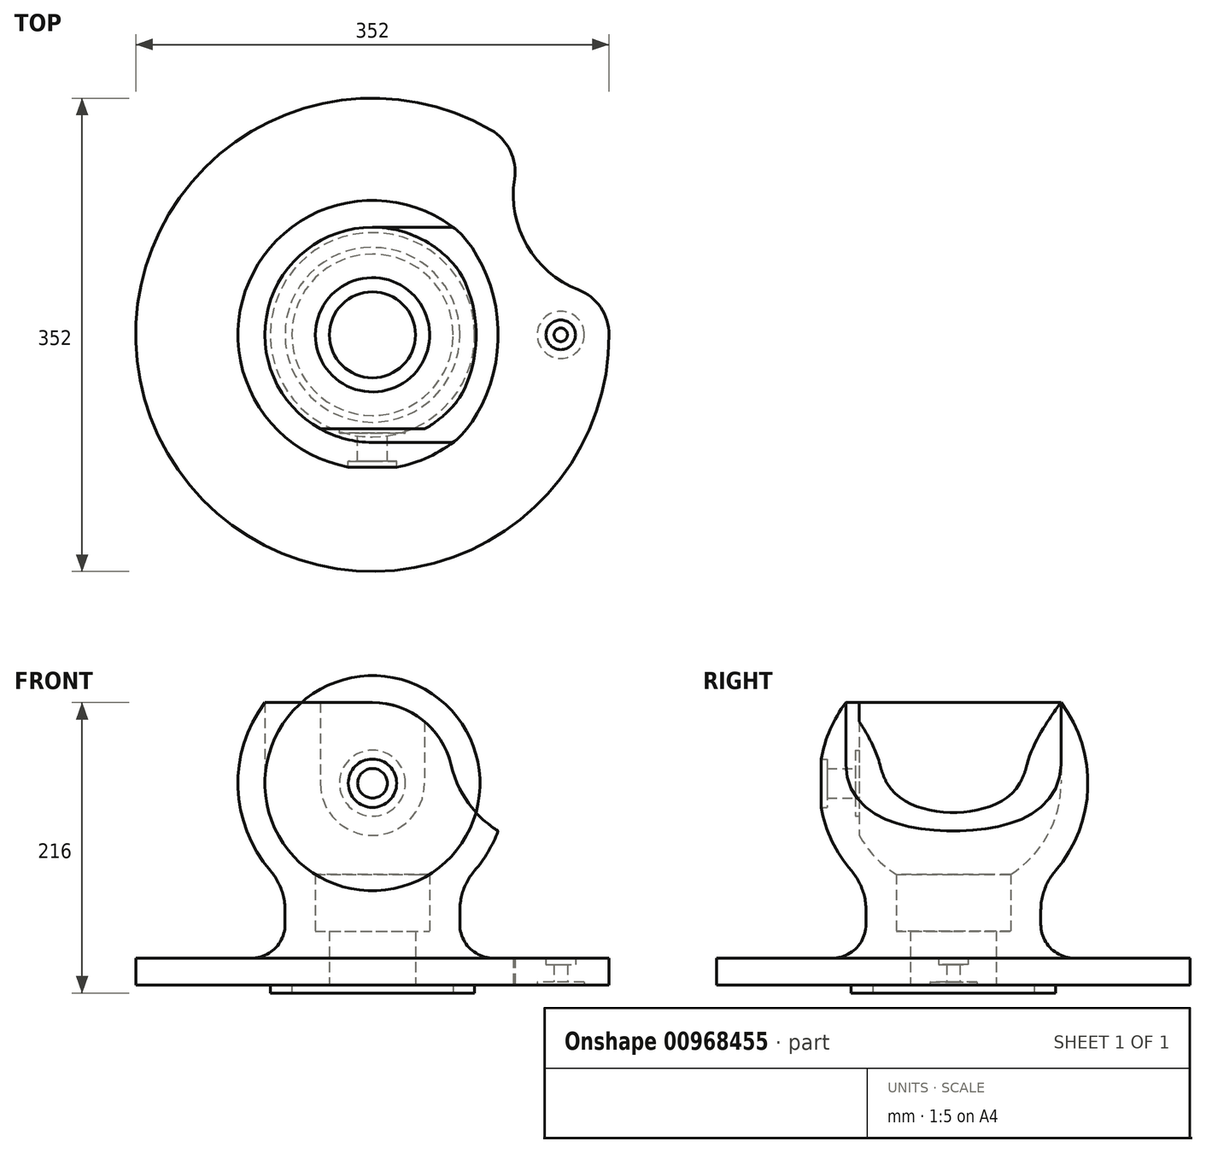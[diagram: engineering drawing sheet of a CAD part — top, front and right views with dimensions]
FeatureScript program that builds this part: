
annotation { "Feature Type Name" : "Feature", "Feature Type Description" : "" }
export const myFeature = defineFeature(function(context is Context, id is Id, definition is map)
    precondition{}
    {
        {
            var Q0;
            Q0=qCreatedBy(makeId("Front.planeOp"),FACE);
            cPlane(context, id + "F0", {"entities" : qUnion([Q0]), "cplaneType" : CPlaneType.OFFSET, "offset" : 100 * mm, "width" : 150 * mm, "height" : 150 * mm});
        }
        {
            var Q0;
            Q0=qCreatedBy(makeId("Front.planeOp"),FACE);
            var sketch = newSketch(context, id + "F1", { "sketchPlane" : qUnion([Q0])});
            skLineSegment(sketch, "E0", {"start": v(32, 0) * mm, "end": v(60, 0) * mm});
            skLineSegment(sketch, "E1", {"start": v(60, 0) * mm, "end": v(60, -6) * mm});
            skLineSegment(sketch, "E2", {"start": v(60, -6) * mm, "end": v(76, -6) * mm});
            skLineSegment(sketch, "E3", {"start": v(76, -6) * mm, "end": v(76, 0) * mm});
            skLineSegment(sketch, "E4", {"start": v(76, 0) * mm, "end": v(176, 0) * mm});
            skLineSegment(sketch, "E5", {"start": v(176, 0) * mm, "end": v(176, 20) * mm});
            skLineSegment(sketch, "E6", {"start": v(176, 20) * mm, "end": v(90, 20) * mm});
            skLineSegment(sketch, "E7", {"start": v(65, 45) * mm, "end": v(65, 55.53) * mm});
            skArc(sketch, "E8", {"start": v(75.86, 84.85) * mm, "mid": v(99.95, 146.7) * mm, "end": v(80, 210) * mm});
            skLineSegment(sketch, "E9", {"start": v(32, 0) * mm, "end": v(32, 40) * mm});
            skLineSegment(sketch, "E10", {"start": v(32, 40) * mm, "end": v(42.5, 40) * mm});
            skLineSegment(sketch, "E11", {"start": v(42.5, 40) * mm, "end": v(42.5, 82.22) * mm});
            skLineSegment(sketch, "E12", {"start": v(80, 210) * mm, "end": v(80, 210) * mm});
            skPoint(sketch, "E13.visualSharp", {"position": v(65, 20) * mm});
            skArc(sketch, "E13.filletArc", {"start": v(65, 45) * mm, "mid": v(72.32, 27.32) * mm, "end": v(90, 20) * mm});
            skPoint(sketch, "E14.visualSharp", {"position": v(65, 74) * mm});
            skArc(sketch, "E14.filletArc", {"start": v(75.86, 84.85) * mm, "mid": v(67.8, 71.16) * mm, "end": v(65, 55.53) * mm});
            skLineSegment(sketch, "E15", {"start": v(0, 0) * mm, "end": v(0, 210) * mm, "construction": true});
            skLineSegment(sketch, "E16", {"start": v(80, 210) * mm, "end": v(80, 150) * mm});
            skArc(sketch, "E17", {"start": v(42.5, 82.22) * mm, "mid": v(70, 111.27) * mm, "end": v(80, 150) * mm});
            skPoint(sketch, "E18.orphan", {"position": v(42.5, 210) * mm});
            skSolve(sketch);
        }
        {
            var Q0;
            Q0=qCreatedBy(makeId("Front.planeOp"),FACE);
            var sketch = newSketch(context, id + "F2", { "sketchPlane" : qUnion([Q0])});
            skArc(sketch, "E19", {"start": v(-40, 150) * mm, "mid": v(0, 110) * mm, "end": v(40, 150) * mm});
            skLineSegment(sketch, "E20", {"start": v(-40, 150) * mm, "end": v(-40, 210) * mm});
            skLineSegment(sketch, "E21", {"start": v(-40, 210) * mm, "end": v(40, 210) * mm});
            skLineSegment(sketch, "E22", {"start": v(40, 210) * mm, "end": v(40, 150) * mm});
            skLineSegment(sketch, "E23.0", {"start": v(80, 210) * mm, "end": v(80, 150) * mm, "construction": true});
            skSolve(sketch);
        }
        {
            var Q0;
            Q0=makeQuery(id+"F1.imprint","IMPRINT",FACE,{"disambiguationData":[TD([[makeQuery(id+"F1.imprint","IMPRINT",EDGE,{"derivedFrom":sQuery(id+"F1.wireOp",EDGE,"E0")}),1.0]])]});
            var Q1;
            Q1=sQuery(id+"F1.wireOp",EDGE,"E15");
            revolve(context, id + "F3", {"surfaceOperationType" : NewSurfaceOperationType.NEW, "entities" : qUnion([Q0]), "axis" : qUnion([Q1]), "revolveType" : RevolveType.FULL});
        }
        {
            var Q0;
            Q0=makeQuery(id+"F2.imprint","IMPRINT",FACE,{"disambiguationData":[TD([[makeQuery(id+"F2.imprint","IMPRINT",EDGE,{"derivedFrom":sQuery(id+"F2.wireOp",EDGE,"E19")}),1.0]])]});
            var Q1;
            Q1=makeQuery(id+"F3.opRevolve","SWEPT_FACE",FACE,{"disambiguationData":[OSD([sQuery(id+"F1.wireOp",EDGE,"E16")])]});
            extrude(context, id + "F4", {"entities" : qUnion([Q0]), "operationType" : NewBodyOperationType.ADD, "endBound" : BoundingType.UP_TO_SURFACE, "depth" : 25 * mm, "endBoundEntityFace" : qUnion([Q1]), "offsetDistance" : 25 * mm, "hasSecondDirection" : true, "secondDirectionOppositeDirection" : false, "secondDirectionDepth" : 70 * mm});
        }
        {
            var Q0;
            Q0=makeQuery(id+"F4.opExtrude","CAP_FACE",FACE,{"disambiguationData":[OSD([sQuery(id+"F2.wireOp",EDGE,"E19"),sQuery(id+"F2.wireOp",EDGE,"E20"),sQuery(id+"F2.wireOp",EDGE,"E21"),sQuery(id+"F2.wireOp",EDGE,"E22")])],"isStart":true});
            var sketch = newSketch(context, id + "F5", { "sketchPlane" : qUnion([Q0])});
            skPoint(sketch, "E24.0", {"position": v(0, 150) * mm});
            skCircle(sketch, "E25", {"center": v(0, 150) * mm, "radius": 24.5 * mm});
            skSolve(sketch);
        }
        {
            var Q0;
            Q0=qCreatedBy(id+"F0.planeOp",FACE);
            var sketch = newSketch(context, id + "F6", { "sketchPlane" : qUnion([Q0])});
            skPoint(sketch, "E26.0", {"position": v(0, 150) * mm});
            skSolve(sketch);
        }
        {
            var Q0;
            Q0=makeQuery(id+"F5.imprint","IMPRINT",FACE,{"disambiguationData":[TD([[makeQuery(id+"F5.imprint","IMPRINT",EDGE,{"derivedFrom":sQuery(id+"F5.wireOp",EDGE,"E25")}),1.0]])]});
            extrude(context, id + "F7", {"entities" : qUnion([Q0]), "operationType" : NewBodyOperationType.REMOVE, "oppositeDirection" : true, "depth" : 3 * mm, "offsetDistance" : 25 * mm});
        }
        {
            var Q0;
            Q0=sQuery(id+"F6.wireOp",VERTEX,"E26.0");
            var Q1;
            Q1=makeQuery(id+"F3.opRevolve","SWEPT_BODY",BODY,{"disambiguationData":[OSD([sQuery(id+"F1.wireOp",EDGE,"E0"),sQuery(id+"F1.wireOp",EDGE,"E1"),sQuery(id+"F1.wireOp",EDGE,"E2"),sQuery(id+"F1.wireOp",EDGE,"E3"),sQuery(id+"F1.wireOp",EDGE,"E4"),sQuery(id+"F1.wireOp",EDGE,"E5"),sQuery(id+"F1.wireOp",EDGE,"E6"),sQuery(id+"F1.wireOp",EDGE,"E7"),sQuery(id+"F1.wireOp",EDGE,"E8"),sQuery(id+"F1.wireOp",EDGE,"E9"),sQuery(id+"F1.wireOp",EDGE,"E10"),sQuery(id+"F1.wireOp",EDGE,"E11"),sQuery(id+"F1.wireOp",EDGE,"E12"),sQuery(id+"F1.wireOp",EDGE,"E13.filletArc"),sQuery(id+"F1.wireOp",EDGE,"E14.filletArc"),sQuery(id+"F1.wireOp",EDGE,"E16"),sQuery(id+"F1.wireOp",EDGE,"E17")])]});
            hole(context, id + "F8", {"style" : HoleStyle.C_BORE, "endStyle" : HoleEndStyle.BLIND, "holeDiameter" : 22 * mm, "cBoreDiameter" : 36 * mm, "cBoreDepth" : 6 * mm, "majorDiameter" : 5 * mm, "holeDepth" : 50 * mm, "isTappedThrough" : true, "tappedDepth" : 29.75 * mm, "tapClearance" : 3, "startFromSketch" : true, "locations" : qUnion([Q0]), "scope" : qUnion([Q1])});
        }
        {
            var Q0;
            Q0=qCreatedBy(makeId("Front.planeOp"),FACE);
            var sketch = newSketch(context, id + "F9", { "sketchPlane" : qUnion([Q0])});
            skArc(sketch, "E27", {"start": v(58.41, 163.71) * mm, "mid": v(0, 210) * mm, "end": v(-58.41, 163.71) * mm});
            skArc(sketch, "E28", {"start": v(58.41, 163.71) * mm, "mid": v(84.18, 121.3) * mm, "end": v(130, 102.25) * mm});
            skArc(sketch, "E29.MirrorCS", {"start": v(-58.41, 163.71) * mm, "mid": v(-84.18, 121.3) * mm, "end": v(-130, 102.25) * mm});
            skLineSegment(sketch, "E30", {"start": v(130, 102.25) * mm, "end": v(130, 210) * mm});
            skLineSegment(sketch, "E31", {"start": v(130, 210) * mm, "end": v(-130, 210) * mm});
            skLineSegment(sketch, "E32", {"start": v(-130, 210) * mm, "end": v(-130, 102.25) * mm});
            skSolve(sketch);
        }
        {
            var Q0;
            {var subQ0=sQuery(id+"F9.wireOp",EDGE,"E28");Q0=makeQuery(id+"F9.imprint","IMPRINT",FACE,{"disambiguationData":[TD([[makeQuery(id+"F9.imprint","IMPRINT",EDGE,{"derivedFrom":subQ0}),1.0]])]});}
            var Q1;
            {var subQ0=sQuery(id+"F9.wireOp",EDGE,"E29.MirrorCS");Q1=makeQuery(id+"F9.imprint","IMPRINT",FACE,{"disambiguationData":[TD([[makeQuery(id+"F9.imprint","IMPRINT",EDGE,{"derivedFrom":subQ0}),-1.0]])]});}
            extrude(context, id + "F10", {"entities" : qUnion([Q0, Q1]), "operationType" : NewBodyOperationType.REMOVE, "oppositeDirection" : true, "depth" : 200 * mm, "offsetDistance" : 25 * mm, "symmetric" : true});
        }
        {
            var Q0;
            Q0=qCreatedBy(makeId("Top.planeOp"),FACE);
            var sketch = newSketch(context, id + "F11", { "sketchPlane" : qUnion([Q0])});
            skArc(sketch, "E33", {"start": v(176, 0) * mm, "mid": v(169.72, 20.3) * mm, "end": v(153.09, 33.54) * mm});
            skArc(sketch, "E34", {"start": v(105.59, 115.8) * mm, "mid": v(102.45, 136.83) * mm, "end": v(88, 152.42) * mm});
            skLineSegment(sketch, "E35", {"start": v(70, 121.24) * mm, "end": v(0, 0) * mm, "construction": true});
            skArc(sketch, "E36", {"start": v(105.59, 115.8) * mm, "mid": v(114.9, 66.34) * mm, "end": v(153.09, 33.54) * mm});
            skArc(sketch, "E37.0", {"start": v(176, 0) * mm, "mid": v(152.42, 88) * mm, "end": v(88, 152.42) * mm});
            skCircle(sketch, "E38", {"center": v(140, 0) * mm, "radius": 17.5 * mm});
            skSolve(sketch);
        }
        {
            var Q0;
            Q0=makeQuery(id+"F11.imprint","IMPRINT",FACE,{"disambiguationData":[TD([[makeQuery(id+"F11.imprint","IMPRINT",EDGE,{"derivedFrom":sQuery(id+"F11.wireOp",EDGE,"E33")}),-1.0]])]});
            extrude(context, id + "F12", {"entities" : qUnion([Q0]), "operationType" : NewBodyOperationType.REMOVE, "endBound" : BoundingType.THROUGH_ALL, "depth" : 25 * mm, "offsetDistance" : 25 * mm});
        }
        {
            var Q0;
            Q0=makeQuery(id+"F11.imprint","IMPRINT",FACE,{"disambiguationData":[TD([[makeQuery(id+"F11.imprint","IMPRINT",EDGE,{"derivedFrom":sQuery(id+"F11.wireOp",EDGE,"E38")}),1.0]])]});
            extrude(context, id + "F13", {"entities" : qUnion([Q0]), "operationType" : NewBodyOperationType.REMOVE, "depth" : 2 * mm, "offsetDistance" : 25 * mm});
        }
        {
            var Q0;
            Q0=makeQuery(id+"F3.opRevolve","SWEPT_FACE",FACE,{"disambiguationData":[OSD([sQuery(id+"F1.wireOp",EDGE,"E6")])]});
            var sketch = newSketch(context, id + "F14", { "sketchPlane" : qUnion([Q0])});
            skPoint(sketch, "E39.0", {"position": v(140, 0) * mm});
            skSolve(sketch);
        }
        {
            var Q0;
            Q0=sQuery(id+"F14.wireOp",VERTEX,"E39.0");
            var Q1;
            Q1=makeQuery(id+"F3.opRevolve","SWEPT_BODY",BODY,{"disambiguationData":[OSD([sQuery(id+"F1.wireOp",EDGE,"E0"),sQuery(id+"F1.wireOp",EDGE,"E1"),sQuery(id+"F1.wireOp",EDGE,"E2"),sQuery(id+"F1.wireOp",EDGE,"E3"),sQuery(id+"F1.wireOp",EDGE,"E4"),sQuery(id+"F1.wireOp",EDGE,"E5"),sQuery(id+"F1.wireOp",EDGE,"E6"),sQuery(id+"F1.wireOp",EDGE,"E7"),sQuery(id+"F1.wireOp",EDGE,"E8"),sQuery(id+"F1.wireOp",EDGE,"E9"),sQuery(id+"F1.wireOp",EDGE,"E10"),sQuery(id+"F1.wireOp",EDGE,"E11"),sQuery(id+"F1.wireOp",EDGE,"E13.filletArc"),sQuery(id+"F1.wireOp",EDGE,"E14.filletArc"),sQuery(id+"F1.wireOp",EDGE,"E16"),sQuery(id+"F1.wireOp",EDGE,"E17")])]});
            hole(context, id + "F15", {"style" : HoleStyle.C_BORE, "endStyle" : HoleEndStyle.THROUGH, "holeDiameter" : 10 * mm, "cBoreDiameter" : 22 * mm, "cBoreDepth" : 5 * mm, "majorDiameter" : 5 * mm, "isTappedThrough" : true, "tappedDepth" : 29.75 * mm, "tapClearance" : 3, "startFromSketch" : true, "locations" : qUnion([Q0]), "scope" : qUnion([Q1])});
        }
    });
